# Revit family: Camera-Conference-Vaddio-Huddle_Shot
name_source: partatom
category: Mechanical Equipment
revit_build: Autodesk Revit 2018 (Build: 20190510_1515(x64)
units: mm (PartAtom-declared; Revit-internal decimal feet)

## family parameters
Always vertical = Yes
Classification = None
Cut with Voids When Loaded = No
OmniClass Number = 23.85.10.17.11
OmniClass Title = Audio-Visual System Components
Part Type = Normal
Room Calculation Point = No
Round Connector Dimension = Use Diameter
Shared = No
Work Plane-Based = No

## types (6) — shared parameters
Assembly Code = D5030
Description = Videoconferencing Camera with Integrated Audio
ENGworks URL = https://ENGworks.com
Edge Radius = 1 109/128"
Family Version = 1.0
Field of View = 125° normal, 110° at full dewarp
Manufacturer = Legrand
Maximum Operating Temperature = 104 °F
Minimum Operating Temperature = 32 °F
Mount Thickness = 9/128"
Operating/Storage Humidity = 20% to 80% RH, non-condensing
Overall Depth = 3 179/256"
Overall Height = 4 31/256"
Overall Width = 24"
Part Description = Videoconferencing Camera with Integrated Audio
Pixels = 2.12 Megapixel (2.42 Total MP)
Power Supply = PoE+
Product Documentation Link = https://res.cloudinary.com
Product Page URL = https://www.legrandav.com
Secondary Depth = 3 83/128"
Secondary Width = 23 243/256"
Standards = CE Approved, FCC Approved
URL = https://www.legrandav.com
Unit Weight = 5.25 lb

## per-type parameters (varying)
| type | Bracket Material | Enclosure Material | Lens Casing Material | Model | Part Number | Speaker Material |
| Gray, North America | Plastic - Gray - Vaddio | Plastic - Gray - Vaddio | Plastic - Dark Gray - Vaddio | 999-50707-000G | 999-50707-000G | Plastic - Med Gray - Vaddio |
| Black, North America | Plastic - Black - Vaddio | Plastic - Black - Vaddio | Plastic - Black - High Gloss - Vaddio | 999-50707-000 | 999-50707-000 | Plastic - Black - Vaddio |
| Gray, Europe | Plastic - Gray - Vaddio | Plastic - Gray - Vaddio | Plastic - Dark Gray - Vaddio | 999-50707-001G | 999-50707-001G | Plastic - Med Gray - Vaddio |
| Gray, Australia/New Zealand | Plastic - Gray - Vaddio | Plastic - Gray - Vaddio | Plastic - Dark Gray - Vaddio | 999-50707-009G | 999-50707-009G | Plastic - Med Gray - Vaddio |
| Black, Europe | Plastic - Black - Vaddio | Plastic - Black - Vaddio | Plastic - Black - High Gloss - Vaddio | 999-50707-001 | 999-50707-001 | Plastic - Black - Vaddio |
| Black, Australia/New Zealand | Plastic - Black - Vaddio | Plastic - Black - Vaddio | Plastic - Black - High Gloss - Vaddio | 999-50707-009 | 999-50707-009 | Plastic - Black - Vaddio |

## geometry (parser evidence)
native form markers: Sweep x3
no freeform markers — native parametric forms only
